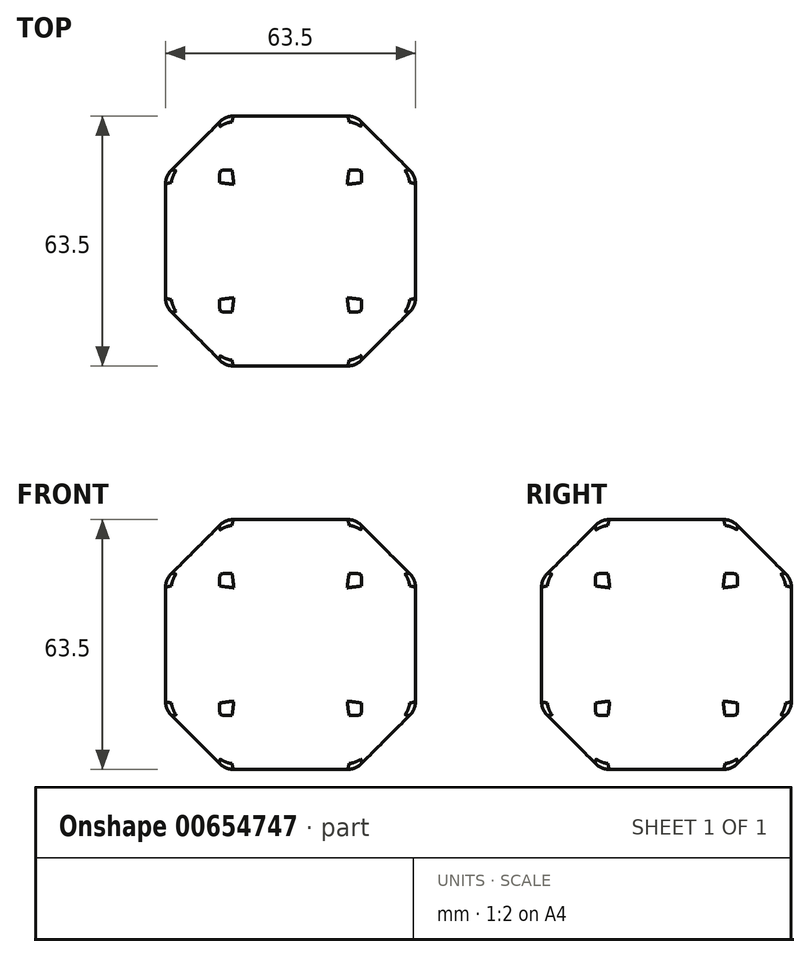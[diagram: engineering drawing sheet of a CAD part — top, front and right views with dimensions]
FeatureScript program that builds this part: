
annotation { "Feature Type Name" : "Feature", "Feature Type Description" : "" }
export const myFeature = defineFeature(function(context is Context, id is Id, definition is map)
    precondition{}
    {
        {
            var Q0;
            Q0=qCreatedBy(makeId("Top.planeOp"),FACE);
            var sketch = newSketch(context, id + "F0", { "sketchPlane" : qUnion([Q0])});
            skLineSegment(sketch, "E0.bottom", {"start": v(-31.75, 31.75) * mm, "end": v(31.75, 31.75) * mm});
            skLineSegment(sketch, "E0.top", {"start": v(-31.75, -31.75) * mm, "end": v(31.75, -31.75) * mm});
            skLineSegment(sketch, "E0.left", {"start": v(-31.75, 31.75) * mm, "end": v(-31.75, -31.75) * mm});
            skLineSegment(sketch, "E0.right", {"start": v(31.75, 31.75) * mm, "end": v(31.75, -31.75) * mm});
            skSolve(sketch);
        }
        {
            var Q0;
            Q0=makeQuery(id+"F0.imprint","IMPRINT",FACE,{"disambiguationData":[TD([[makeQuery(id+"F0.imprint","IMPRINT",EDGE,{"derivedFrom":sQuery(id+"F0.wireOp",EDGE,"E0.bottom")}),-1.0]])]});
            extrude(context, id + "F1", {"entities" : qUnion([Q0]), "depth" : 31.75 * mm, "offsetDistance" : 25.4 * mm, "hasSecondDirection" : true, "secondDirectionOppositeDirection" : true, "secondDirectionDepth" : 31.75 * mm});
        }
        {
            var Q0;
            Q0=makeQuery(id+"F1.opExtrude","CAP_EDGE",EDGE,{"disambiguationData":[OSD([sQuery(id+"F0.wireOp",EDGE,"E0.right")])],"isStart":false});
            var Q1;
            Q1=makeQuery(id+"F1.opExtrude","CAP_EDGE",EDGE,{"disambiguationData":[OSD([sQuery(id+"F0.wireOp",EDGE,"E0.top")])],"isStart":false});
            var Q2;
            Q2=makeQuery(id+"F1.opExtrude","CAP_EDGE",EDGE,{"disambiguationData":[OSD([sQuery(id+"F0.wireOp",EDGE,"E0.left")])],"isStart":false});
            var Q3;
            Q3=makeQuery(id+"F1.opExtrude","CAP_EDGE",EDGE,{"disambiguationData":[OSD([sQuery(id+"F0.wireOp",EDGE,"E0.bottom")])],"isStart":false});
            var Q4;
            Q4=makeQuery(id+"F1.opExtrude","CAP_EDGE",EDGE,{"disambiguationData":[OSD([sQuery(id+"F0.wireOp",EDGE,"E0.top")])],"isStart":true});
            var Q5;
            Q5=makeQuery(id+"F1.opExtrude","CAP_EDGE",EDGE,{"disambiguationData":[OSD([sQuery(id+"F0.wireOp",EDGE,"E0.right")])],"isStart":true});
            var Q6;
            Q6=makeQuery(id+"F1.opExtrude","CAP_EDGE",EDGE,{"disambiguationData":[OSD([sQuery(id+"F0.wireOp",EDGE,"E0.bottom")])],"isStart":true});
            var Q7;
            Q7=makeQuery(id+"F1.opExtrude","CAP_EDGE",EDGE,{"disambiguationData":[OSD([sQuery(id+"F0.wireOp",EDGE,"E0.left")])],"isStart":true});
            var Q8;
            Q8=makeQuery(id+"F1.opExtrude","SWEPT_EDGE",EDGE,{"disambiguationData":[OSD([sQuery(id+"F0.wireOp",EDGE,"E0.bottom"),sQuery(id+"F0.wireOp",EDGE,"E0.left")])]});
            var Q9;
            Q9=makeQuery(id+"F1.opExtrude","SWEPT_EDGE",EDGE,{"disambiguationData":[OSD([sQuery(id+"F0.wireOp",EDGE,"E0.bottom"),sQuery(id+"F0.wireOp",EDGE,"E0.right")])]});
            var Q10;
            Q10=makeQuery(id+"F1.opExtrude","SWEPT_EDGE",EDGE,{"disambiguationData":[OSD([sQuery(id+"F0.wireOp",EDGE,"E0.top"),sQuery(id+"F0.wireOp",EDGE,"E0.right")])]});
            var Q11;
            Q11=makeQuery(id+"F1.opExtrude","SWEPT_EDGE",EDGE,{"disambiguationData":[OSD([sQuery(id+"F0.wireOp",EDGE,"E0.top"),sQuery(id+"F0.wireOp",EDGE,"E0.left")])]});
            chamfer(context, id + "F2", {"entities" : qUnion([Q0, Q1, Q2, Q3, Q4, Q5, Q6, Q7, Q8, Q9, Q10, Q11]), "width" : 15.24 * mm, "tangentPropagation" : true});
        }
        {
            var Q0;
            {var subQ0=sQuery(id+"F0.wireOp",EDGE,"E0.left");Q0=makeQuery(id+"F2.opChamfer","BLEND_EDGE",EDGE,{"blendedFrom":[makeQuery(id+"F1.opExtrude","CAP_VERTEX",VERTEX,{"disambiguationData":[OSD([sQuery(id+"F0.wireOp",EDGE,"E0.bottom"),subQ0])],"isStart":false}),makeQuery(id+"F1.opExtrude","CAP_EDGE",EDGE,{"disambiguationData":[OSD([subQ0])],"isStart":false})],"blendedInto":[]});}
            var Q1;
            {var subQ0=sQuery(id+"F0.wireOp",EDGE,"E0.left");var subQ1=sQuery(id+"F0.wireOp",EDGE,"E0.bottom");Q1=makeQuery(id+"F2.opChamfer","BLEND_FACE",FACE,{"disambiguationData":[OSD([subQ1,subQ0]),TDD([makeQuery(id+"F1.opExtrude","CAP_VERTEX",VERTEX,{"disambiguationData":[OSD([subQ1,subQ0])],"isStart":false})])]});}
            var Q2;
            {var subQ0=sQuery(id+"F0.wireOp",EDGE,"E0.left");var subQ1=sQuery(id+"F0.wireOp",EDGE,"E0.bottom");Q2=makeQuery(id+"F2.opChamfer","BLEND_EDGE",EDGE,{"blendedFrom":[makeQuery(id+"F1.opExtrude","CAP_VERTEX",VERTEX,{"disambiguationData":[OSD([subQ1,subQ0])],"isStart":false}),makeQuery(id+"F1.opExtrude","SWEPT_EDGE",EDGE,{"disambiguationData":[OSD([subQ1,subQ0])]})],"blendedInto":[]});}
            var Q3;
            {var subQ0=sQuery(id+"F0.wireOp",EDGE,"E0.right");var subQ1=sQuery(id+"F0.wireOp",EDGE,"E0.bottom");Q3=makeQuery(id+"F2.opChamfer","BLEND_FACE",FACE,{"disambiguationData":[OSD([subQ1,subQ0]),TDD([makeQuery(id+"F1.opExtrude","CAP_VERTEX",VERTEX,{"disambiguationData":[OSD([subQ1,subQ0])],"isStart":true})])]});}
            var Q4;
            {var subQ0=sQuery(id+"F0.wireOp",EDGE,"E0.right");var subQ1=sQuery(id+"F0.wireOp",EDGE,"E0.bottom");Q4=makeQuery(id+"F2.opChamfer","BLEND_FACE",FACE,{"disambiguationData":[OSD([subQ1,subQ0]),TDD([makeQuery(id+"F1.opExtrude","CAP_VERTEX",VERTEX,{"disambiguationData":[OSD([subQ1,subQ0])],"isStart":false})])]});}
            var Q5;
            {var subQ0=sQuery(id+"F0.wireOp",EDGE,"E0.bottom");Q5=makeQuery(id+"F2.opChamfer","BLEND_EDGE",EDGE,{"blendedFrom":[makeQuery(id+"F1.opExtrude","CAP_VERTEX",VERTEX,{"disambiguationData":[OSD([subQ0,sQuery(id+"F0.wireOp",EDGE,"E0.left")])],"isStart":false}),makeQuery(id+"F1.opExtrude","CAP_EDGE",EDGE,{"disambiguationData":[OSD([subQ0])],"isStart":false})],"blendedInto":[]});}
            var Q6;
            {var subQ0=sQuery(id+"F0.wireOp",EDGE,"E0.bottom");Q6=makeQuery(id+"F2.opChamfer","BLEND_FACE",FACE,{"disambiguationData":[OSD([subQ0]),TDD([makeQuery(id+"F1.opExtrude","CAP_EDGE",EDGE,{"disambiguationData":[OSD([subQ0])],"isStart":false})])]});}
            var Q7;
            {var subQ0=sQuery(id+"F0.wireOp",EDGE,"E0.top");Q7=makeQuery(id+"F2.opChamfer","BLEND_FACE",FACE,{"disambiguationData":[OSD([subQ0]),TDD([makeQuery(id+"F1.opExtrude","CAP_EDGE",EDGE,{"disambiguationData":[OSD([subQ0])],"isStart":false})])]});}
            var Q8;
            {var subQ0=sQuery(id+"F0.wireOp",EDGE,"E0.left");var subQ1=sQuery(id+"F0.wireOp",EDGE,"E0.top");Q8=makeQuery(id+"F2.opChamfer","BLEND_FACE",FACE,{"disambiguationData":[OSD([subQ1,subQ0]),TDD([makeQuery(id+"F1.opExtrude","CAP_VERTEX",VERTEX,{"disambiguationData":[OSD([subQ1,subQ0])],"isStart":false})])]});}
            var Q9;
            {var subQ0=sQuery(id+"F0.wireOp",EDGE,"E0.right");var subQ1=sQuery(id+"F0.wireOp",EDGE,"E0.top");Q9=makeQuery(id+"F2.opChamfer","BLEND_FACE",FACE,{"disambiguationData":[OSD([subQ1,subQ0]),TDD([makeQuery(id+"F1.opExtrude","CAP_VERTEX",VERTEX,{"disambiguationData":[OSD([subQ1,subQ0])],"isStart":true})])]});}
            var Q10;
            {var subQ0=sQuery(id+"F0.wireOp",EDGE,"E0.bottom");Q10=makeQuery(id+"F2.opChamfer","BLEND_EDGE",EDGE,{"blendedFrom":[makeQuery(id+"F1.opExtrude","CAP_VERTEX",VERTEX,{"disambiguationData":[OSD([subQ0,sQuery(id+"F0.wireOp",EDGE,"E0.right")])],"isStart":true}),makeQuery(id+"F1.opExtrude","CAP_EDGE",EDGE,{"disambiguationData":[OSD([subQ0])],"isStart":true})],"blendedInto":[]});}
            var Q11;
            {var subQ0=sQuery(id+"F0.wireOp",EDGE,"E0.right");var subQ1=sQuery(id+"F0.wireOp",EDGE,"E0.top");Q11=makeQuery(id+"F2.opChamfer","BLEND_FACE",FACE,{"disambiguationData":[OSD([subQ1,subQ0]),TDD([makeQuery(id+"F1.opExtrude","CAP_VERTEX",VERTEX,{"disambiguationData":[OSD([subQ1,subQ0])],"isStart":false})])]});}
            var Q12;
            {var subQ0=sQuery(id+"F0.wireOp",EDGE,"E0.right");Q12=makeQuery(id+"F2.opChamfer","BLEND_EDGE",EDGE,{"blendedFrom":[makeQuery(id+"F1.opExtrude","CAP_VERTEX",VERTEX,{"disambiguationData":[OSD([sQuery(id+"F0.wireOp",EDGE,"E0.bottom"),subQ0])],"isStart":true}),makeQuery(id+"F1.opExtrude","CAP_EDGE",EDGE,{"disambiguationData":[OSD([subQ0])],"isStart":true})],"blendedInto":[]});}
            var Q13;
            {var subQ0=sQuery(id+"F0.wireOp",EDGE,"E0.right");var subQ1=sQuery(id+"F0.wireOp",EDGE,"E0.bottom");Q13=makeQuery(id+"F2.opChamfer","BLEND_FACE",FACE,{"disambiguationData":[OSD([subQ1,subQ0]),TDD([makeQuery(id+"F1.opExtrude","SWEPT_EDGE",EDGE,{"disambiguationData":[OSD([subQ1,subQ0])]})])]});}
            var Q14;
            {var subQ0=sQuery(id+"F0.wireOp",EDGE,"E0.bottom");Q14=makeQuery(id+"F2.opChamfer","BLEND_EDGE",EDGE,{"blendedFrom":[makeQuery(id+"F1.opExtrude","CAP_VERTEX",VERTEX,{"disambiguationData":[OSD([subQ0,sQuery(id+"F0.wireOp",EDGE,"E0.right")])],"isStart":false}),makeQuery(id+"F1.opExtrude","CAP_EDGE",EDGE,{"disambiguationData":[OSD([subQ0])],"isStart":false})],"blendedInto":[]});}
            var Q15;
            {var subQ0=sQuery(id+"F0.wireOp",EDGE,"E0.right");Q15=makeQuery(id+"F2.opChamfer","BLEND_EDGE",EDGE,{"blendedFrom":[makeQuery(id+"F1.opExtrude","CAP_VERTEX",VERTEX,{"disambiguationData":[OSD([sQuery(id+"F0.wireOp",EDGE,"E0.bottom"),subQ0])],"isStart":false}),makeQuery(id+"F1.opExtrude","CAP_EDGE",EDGE,{"disambiguationData":[OSD([subQ0])],"isStart":false})],"blendedInto":[]});}
            var Q16;
            {var subQ0=sQuery(id+"F0.wireOp",EDGE,"E0.right");var subQ1=sQuery(id+"F0.wireOp",EDGE,"E0.top");Q16=makeQuery(id+"F2.opChamfer","BLEND_FACE",FACE,{"disambiguationData":[OSD([subQ1,subQ0]),TDD([makeQuery(id+"F1.opExtrude","SWEPT_EDGE",EDGE,{"disambiguationData":[OSD([subQ1,subQ0])]})])]});}
            var Q17;
            {var subQ0=sQuery(id+"F0.wireOp",EDGE,"E0.bottom");Q17=makeQuery(id+"F2.opChamfer","BLEND_FACE",FACE,{"disambiguationData":[OSD([subQ0]),TDD([makeQuery(id+"F1.opExtrude","CAP_EDGE",EDGE,{"disambiguationData":[OSD([subQ0])],"isStart":true})])]});}
            var Q18;
            {var subQ0=sQuery(id+"F0.wireOp",EDGE,"E0.right");Q18=makeQuery(id+"F2.opChamfer","BLEND_EDGE",EDGE,{"blendedFrom":[makeQuery(id+"F1.opExtrude","CAP_EDGE",EDGE,{"disambiguationData":[OSD([subQ0])],"isStart":true}),makeQuery(id+"F1.opExtrude","SWEPT_FACE",FACE,{"disambiguationData":[OSD([subQ0])]})],"blendedInto":[makeQuery(id+"F1.opExtrude","SWEPT_FACE",FACE,{"disambiguationData":[OSD([subQ0])]})]});}
            var Q19;
            {var subQ0=sQuery(id+"F0.wireOp",EDGE,"E0.right");Q19=makeQuery(id+"F2.opChamfer","BLEND_EDGE",EDGE,{"blendedFrom":[makeQuery(id+"F1.opExtrude","CAP_EDGE",EDGE,{"disambiguationData":[OSD([subQ0])],"isStart":false}),makeQuery(id+"F1.opExtrude","CAP_FACE",FACE,{"disambiguationData":[OSD([sQuery(id+"F0.wireOp",EDGE,"E0.bottom"),sQuery(id+"F0.wireOp",EDGE,"E0.top"),sQuery(id+"F0.wireOp",EDGE,"E0.left"),subQ0])],"isStart":false})],"blendedInto":[makeQuery(id+"F1.opExtrude","CAP_FACE",FACE,{"disambiguationData":[OSD([sQuery(id+"F0.wireOp",EDGE,"E0.bottom"),sQuery(id+"F0.wireOp",EDGE,"E0.top"),sQuery(id+"F0.wireOp",EDGE,"E0.left"),subQ0])],"isStart":false})]});}
            var Q20;
            {var subQ0=sQuery(id+"F0.wireOp",EDGE,"E0.right");Q20=makeQuery(id+"F2.opChamfer","BLEND_EDGE",EDGE,{"blendedFrom":[makeQuery(id+"F1.opExtrude","CAP_EDGE",EDGE,{"disambiguationData":[OSD([subQ0])],"isStart":false}),makeQuery(id+"F1.opExtrude","SWEPT_FACE",FACE,{"disambiguationData":[OSD([subQ0])]})],"blendedInto":[makeQuery(id+"F1.opExtrude","SWEPT_FACE",FACE,{"disambiguationData":[OSD([subQ0])]})]});}
            var Q21;
            {var subQ0=sQuery(id+"F0.wireOp",EDGE,"E0.top");Q21=makeQuery(id+"F2.opChamfer","BLEND_EDGE",EDGE,{"blendedFrom":[makeQuery(id+"F1.opExtrude","CAP_VERTEX",VERTEX,{"disambiguationData":[OSD([subQ0,sQuery(id+"F0.wireOp",EDGE,"E0.left")])],"isStart":false}),makeQuery(id+"F1.opExtrude","CAP_EDGE",EDGE,{"disambiguationData":[OSD([subQ0])],"isStart":false})],"blendedInto":[]});}
            var Q22;
            {var subQ0=sQuery(id+"F0.wireOp",EDGE,"E0.bottom");Q22=makeQuery(id+"F2.opChamfer","BLEND_EDGE",EDGE,{"blendedFrom":[makeQuery(id+"F1.opExtrude","CAP_EDGE",EDGE,{"disambiguationData":[OSD([subQ0])],"isStart":true}),makeQuery(id+"F1.opExtrude","SWEPT_FACE",FACE,{"disambiguationData":[OSD([subQ0])]})],"blendedInto":[makeQuery(id+"F1.opExtrude","SWEPT_FACE",FACE,{"disambiguationData":[OSD([subQ0])]})]});}
            var Q23;
            {var subQ0=sQuery(id+"F0.wireOp",EDGE,"E0.right");var subQ1=sQuery(id+"F0.wireOp",EDGE,"E0.top");Q23=makeQuery(id+"F2.opChamfer","BLEND_EDGE",EDGE,{"blendedFrom":[makeQuery(id+"F1.opExtrude","CAP_VERTEX",VERTEX,{"disambiguationData":[OSD([subQ1,subQ0])],"isStart":true}),makeQuery(id+"F1.opExtrude","SWEPT_EDGE",EDGE,{"disambiguationData":[OSD([subQ1,subQ0])]})],"blendedInto":[]});}
            var Q24;
            {var subQ0=sQuery(id+"F0.wireOp",EDGE,"E0.bottom");Q24=makeQuery(id+"F2.opChamfer","BLEND_EDGE",EDGE,{"blendedFrom":[makeQuery(id+"F1.opExtrude","CAP_EDGE",EDGE,{"disambiguationData":[OSD([subQ0])],"isStart":false}),makeQuery(id+"F1.opExtrude","SWEPT_FACE",FACE,{"disambiguationData":[OSD([subQ0])]})],"blendedInto":[makeQuery(id+"F1.opExtrude","SWEPT_FACE",FACE,{"disambiguationData":[OSD([subQ0])]})]});}
            var Q25;
            {var subQ0=sQuery(id+"F0.wireOp",EDGE,"E0.right");Q25=makeQuery(id+"F2.opChamfer","BLEND_FACE",FACE,{"disambiguationData":[OSD([subQ0]),TDD([makeQuery(id+"F1.opExtrude","CAP_EDGE",EDGE,{"disambiguationData":[OSD([subQ0])],"isStart":true})])]});}
            var Q26;
            {var subQ0=sQuery(id+"F0.wireOp",EDGE,"E0.bottom");Q26=makeQuery(id+"F2.opChamfer","BLEND_EDGE",EDGE,{"blendedFrom":[makeQuery(id+"F1.opExtrude","CAP_EDGE",EDGE,{"disambiguationData":[OSD([subQ0])],"isStart":false}),makeQuery(id+"F1.opExtrude","CAP_FACE",FACE,{"disambiguationData":[OSD([subQ0,sQuery(id+"F0.wireOp",EDGE,"E0.top"),sQuery(id+"F0.wireOp",EDGE,"E0.left"),sQuery(id+"F0.wireOp",EDGE,"E0.right")])],"isStart":false})],"blendedInto":[makeQuery(id+"F1.opExtrude","CAP_FACE",FACE,{"disambiguationData":[OSD([subQ0,sQuery(id+"F0.wireOp",EDGE,"E0.top"),sQuery(id+"F0.wireOp",EDGE,"E0.left"),sQuery(id+"F0.wireOp",EDGE,"E0.right")])],"isStart":false})]});}
            var Q27;
            {var subQ0=sQuery(id+"F0.wireOp",EDGE,"E0.right");Q27=makeQuery(id+"F2.opChamfer","BLEND_FACE",FACE,{"disambiguationData":[OSD([subQ0]),TDD([makeQuery(id+"F1.opExtrude","CAP_EDGE",EDGE,{"disambiguationData":[OSD([subQ0])],"isStart":false})])]});}
            var Q28;
            {var subQ0=sQuery(id+"F0.wireOp",EDGE,"E0.right");Q28=makeQuery(id+"F2.opChamfer","BLEND_EDGE",EDGE,{"blendedFrom":[makeQuery(id+"F1.opExtrude","CAP_VERTEX",VERTEX,{"disambiguationData":[OSD([sQuery(id+"F0.wireOp",EDGE,"E0.top"),subQ0])],"isStart":true}),makeQuery(id+"F1.opExtrude","CAP_EDGE",EDGE,{"disambiguationData":[OSD([subQ0])],"isStart":true})],"blendedInto":[]});}
            var Q29;
            Q29=makeQuery(id+"F1.opExtrude","SWEPT_FACE",FACE,{"disambiguationData":[OSD([sQuery(id+"F0.wireOp",EDGE,"E0.bottom")])]});
            var Q30;
            {var subQ0=sQuery(id+"F0.wireOp",EDGE,"E0.right");var subQ1=sQuery(id+"F0.wireOp",EDGE,"E0.top");Q30=makeQuery(id+"F2.opChamfer","BLEND_EDGE",EDGE,{"blendedFrom":[makeQuery(id+"F1.opExtrude","CAP_VERTEX",VERTEX,{"disambiguationData":[OSD([subQ1,subQ0])],"isStart":false}),makeQuery(id+"F1.opExtrude","SWEPT_EDGE",EDGE,{"disambiguationData":[OSD([subQ1,subQ0])]})],"blendedInto":[]});}
            var Q31;
            {var subQ0=sQuery(id+"F0.wireOp",EDGE,"E0.top");Q31=makeQuery(id+"F2.opChamfer","BLEND_EDGE",EDGE,{"blendedFrom":[makeQuery(id+"F1.opExtrude","CAP_VERTEX",VERTEX,{"disambiguationData":[OSD([subQ0,sQuery(id+"F0.wireOp",EDGE,"E0.right")])],"isStart":false}),makeQuery(id+"F1.opExtrude","CAP_EDGE",EDGE,{"disambiguationData":[OSD([subQ0])],"isStart":false})],"blendedInto":[]});}
            var Q32;
            {var subQ0=sQuery(id+"F0.wireOp",EDGE,"E0.top");Q32=makeQuery(id+"F2.opChamfer","BLEND_EDGE",EDGE,{"blendedFrom":[makeQuery(id+"F1.opExtrude","CAP_EDGE",EDGE,{"disambiguationData":[OSD([subQ0])],"isStart":false}),makeQuery(id+"F1.opExtrude","CAP_FACE",FACE,{"disambiguationData":[OSD([sQuery(id+"F0.wireOp",EDGE,"E0.bottom"),subQ0,sQuery(id+"F0.wireOp",EDGE,"E0.left"),sQuery(id+"F0.wireOp",EDGE,"E0.right")])],"isStart":false})],"blendedInto":[makeQuery(id+"F1.opExtrude","CAP_FACE",FACE,{"disambiguationData":[OSD([sQuery(id+"F0.wireOp",EDGE,"E0.bottom"),subQ0,sQuery(id+"F0.wireOp",EDGE,"E0.left"),sQuery(id+"F0.wireOp",EDGE,"E0.right")])],"isStart":false})]});}
            var Q33;
            Q33=makeQuery(id+"F1.opExtrude","CAP_FACE",FACE,{"disambiguationData":[OSD([sQuery(id+"F0.wireOp",EDGE,"E0.bottom"),sQuery(id+"F0.wireOp",EDGE,"E0.top"),sQuery(id+"F0.wireOp",EDGE,"E0.left"),sQuery(id+"F0.wireOp",EDGE,"E0.right")])],"isStart":false});
            var Q34;
            {var subQ0=sQuery(id+"F0.wireOp",EDGE,"E0.right");Q34=makeQuery(id+"F2.opChamfer","BLEND_EDGE",EDGE,{"blendedFrom":[makeQuery(id+"F1.opExtrude","CAP_VERTEX",VERTEX,{"disambiguationData":[OSD([sQuery(id+"F0.wireOp",EDGE,"E0.top"),subQ0])],"isStart":false}),makeQuery(id+"F1.opExtrude","CAP_EDGE",EDGE,{"disambiguationData":[OSD([subQ0])],"isStart":false})],"blendedInto":[]});}
            var Q35;
            {var subQ0=sQuery(id+"F0.wireOp",EDGE,"E0.top");Q35=makeQuery(id+"F2.opChamfer","BLEND_EDGE",EDGE,{"blendedFrom":[makeQuery(id+"F1.opExtrude","CAP_EDGE",EDGE,{"disambiguationData":[OSD([subQ0])],"isStart":false}),makeQuery(id+"F1.opExtrude","SWEPT_FACE",FACE,{"disambiguationData":[OSD([subQ0])]})],"blendedInto":[makeQuery(id+"F1.opExtrude","SWEPT_FACE",FACE,{"disambiguationData":[OSD([subQ0])]})]});}
            var Q36;
            Q36=makeQuery(id+"F1.opExtrude","SWEPT_FACE",FACE,{"disambiguationData":[OSD([sQuery(id+"F0.wireOp",EDGE,"E0.top")])]});
            var Q37;
            Q37=makeQuery(id+"F1.opExtrude","SWEPT_FACE",FACE,{"disambiguationData":[OSD([sQuery(id+"F0.wireOp",EDGE,"E0.right")])]});
            var Q38;
            {var subQ0=sQuery(id+"F0.wireOp",EDGE,"E0.left");Q38=makeQuery(id+"F2.opChamfer","BLEND_EDGE",EDGE,{"blendedFrom":[makeQuery(id+"F1.opExtrude","CAP_EDGE",EDGE,{"disambiguationData":[OSD([subQ0])],"isStart":false}),makeQuery(id+"F1.opExtrude","CAP_FACE",FACE,{"disambiguationData":[OSD([sQuery(id+"F0.wireOp",EDGE,"E0.bottom"),sQuery(id+"F0.wireOp",EDGE,"E0.top"),subQ0,sQuery(id+"F0.wireOp",EDGE,"E0.right")])],"isStart":false})],"blendedInto":[makeQuery(id+"F1.opExtrude","CAP_FACE",FACE,{"disambiguationData":[OSD([sQuery(id+"F0.wireOp",EDGE,"E0.bottom"),sQuery(id+"F0.wireOp",EDGE,"E0.top"),subQ0,sQuery(id+"F0.wireOp",EDGE,"E0.right")])],"isStart":false})]});}
            var Q39;
            {var subQ0=sQuery(id+"F0.wireOp",EDGE,"E0.right");Q39=makeQuery(id+"F2.opChamfer","BLEND_EDGE",EDGE,{"blendedFrom":[makeQuery(id+"F1.opExtrude","CAP_EDGE",EDGE,{"disambiguationData":[OSD([subQ0])],"isStart":true}),makeQuery(id+"F1.opExtrude","CAP_FACE",FACE,{"disambiguationData":[OSD([sQuery(id+"F0.wireOp",EDGE,"E0.bottom"),sQuery(id+"F0.wireOp",EDGE,"E0.top"),sQuery(id+"F0.wireOp",EDGE,"E0.left"),subQ0])],"isStart":true})],"blendedInto":[makeQuery(id+"F1.opExtrude","CAP_FACE",FACE,{"disambiguationData":[OSD([sQuery(id+"F0.wireOp",EDGE,"E0.bottom"),sQuery(id+"F0.wireOp",EDGE,"E0.top"),sQuery(id+"F0.wireOp",EDGE,"E0.left"),subQ0])],"isStart":true})]});}
            var Q40;
            {var subQ0=sQuery(id+"F0.wireOp",EDGE,"E0.left");var subQ1=sQuery(id+"F0.wireOp",EDGE,"E0.top");Q40=makeQuery(id+"F2.opChamfer","BLEND_FACE",FACE,{"disambiguationData":[OSD([subQ1,subQ0]),TDD([makeQuery(id+"F1.opExtrude","CAP_VERTEX",VERTEX,{"disambiguationData":[OSD([subQ1,subQ0])],"isStart":true})])]});}
            var Q41;
            {var subQ0=sQuery(id+"F0.wireOp",EDGE,"E0.left");Q41=makeQuery(id+"F2.opChamfer","BLEND_EDGE",EDGE,{"blendedFrom":[makeQuery(id+"F1.opExtrude","CAP_VERTEX",VERTEX,{"disambiguationData":[OSD([sQuery(id+"F0.wireOp",EDGE,"E0.bottom"),subQ0])],"isStart":true}),makeQuery(id+"F1.opExtrude","CAP_EDGE",EDGE,{"disambiguationData":[OSD([subQ0])],"isStart":true})],"blendedInto":[]});}
            var Q42;
            {var subQ0=sQuery(id+"F0.wireOp",EDGE,"E0.bottom");Q42=makeQuery(id+"F2.opChamfer","BLEND_EDGE",EDGE,{"blendedFrom":[makeQuery(id+"F1.opExtrude","CAP_VERTEX",VERTEX,{"disambiguationData":[OSD([subQ0,sQuery(id+"F0.wireOp",EDGE,"E0.left")])],"isStart":true}),makeQuery(id+"F1.opExtrude","CAP_EDGE",EDGE,{"disambiguationData":[OSD([subQ0])],"isStart":true})],"blendedInto":[]});}
            var Q43;
            {var subQ0=sQuery(id+"F0.wireOp",EDGE,"E0.left");var subQ1=sQuery(id+"F0.wireOp",EDGE,"E0.bottom");Q43=makeQuery(id+"F2.opChamfer","BLEND_FACE",FACE,{"disambiguationData":[OSD([subQ1,subQ0]),TDD([makeQuery(id+"F1.opExtrude","CAP_VERTEX",VERTEX,{"disambiguationData":[OSD([subQ1,subQ0])],"isStart":true})])]});}
            var Q44;
            {var subQ0=sQuery(id+"F0.wireOp",EDGE,"E0.left");var subQ1=sQuery(id+"F0.wireOp",EDGE,"E0.bottom");Q44=makeQuery(id+"F2.opChamfer","BLEND_EDGE",EDGE,{"blendedFrom":[makeQuery(id+"F1.opExtrude","CAP_VERTEX",VERTEX,{"disambiguationData":[OSD([subQ1,subQ0])],"isStart":true}),makeQuery(id+"F1.opExtrude","SWEPT_EDGE",EDGE,{"disambiguationData":[OSD([subQ1,subQ0])]})],"blendedInto":[]});}
            var Q45;
            {var subQ0=sQuery(id+"F0.wireOp",EDGE,"E0.top");Q45=makeQuery(id+"F2.opChamfer","BLEND_FACE",FACE,{"disambiguationData":[OSD([subQ0]),TDD([makeQuery(id+"F1.opExtrude","CAP_EDGE",EDGE,{"disambiguationData":[OSD([subQ0])],"isStart":true})])]});}
            var Q46;
            {var subQ0=sQuery(id+"F0.wireOp",EDGE,"E0.left");Q46=makeQuery(id+"F2.opChamfer","BLEND_EDGE",EDGE,{"blendedFrom":[makeQuery(id+"F1.opExtrude","CAP_VERTEX",VERTEX,{"disambiguationData":[OSD([sQuery(id+"F0.wireOp",EDGE,"E0.top"),subQ0])],"isStart":true}),makeQuery(id+"F1.opExtrude","CAP_EDGE",EDGE,{"disambiguationData":[OSD([subQ0])],"isStart":true})],"blendedInto":[]});}
            var Q47;
            {var subQ0=sQuery(id+"F0.wireOp",EDGE,"E0.top");Q47=makeQuery(id+"F2.opChamfer","BLEND_EDGE",EDGE,{"blendedFrom":[makeQuery(id+"F1.opExtrude","CAP_VERTEX",VERTEX,{"disambiguationData":[OSD([subQ0,sQuery(id+"F0.wireOp",EDGE,"E0.left")])],"isStart":true}),makeQuery(id+"F1.opExtrude","CAP_EDGE",EDGE,{"disambiguationData":[OSD([subQ0])],"isStart":true})],"blendedInto":[]});}
            var Q48;
            {var subQ0=sQuery(id+"F0.wireOp",EDGE,"E0.right");var subQ1=sQuery(id+"F0.wireOp",EDGE,"E0.bottom");Q48=makeQuery(id+"F2.opChamfer","BLEND_EDGE",EDGE,{"blendedFrom":[makeQuery(id+"F1.opExtrude","CAP_VERTEX",VERTEX,{"disambiguationData":[OSD([subQ1,subQ0])],"isStart":true}),makeQuery(id+"F1.opExtrude","SWEPT_EDGE",EDGE,{"disambiguationData":[OSD([subQ1,subQ0])]})],"blendedInto":[]});}
            var Q49;
            {var subQ0=sQuery(id+"F0.wireOp",EDGE,"E0.left");var subQ1=sQuery(id+"F0.wireOp",EDGE,"E0.bottom");Q49=makeQuery(id+"F2.opChamfer","BLEND_FACE",FACE,{"disambiguationData":[OSD([subQ1,subQ0]),TDD([makeQuery(id+"F1.opExtrude","SWEPT_EDGE",EDGE,{"disambiguationData":[OSD([subQ1,subQ0])]})])]});}
            var Q50;
            {var subQ0=sQuery(id+"F0.wireOp",EDGE,"E0.right");var subQ1=sQuery(id+"F0.wireOp",EDGE,"E0.bottom");Q50=makeQuery(id+"F2.opChamfer","BLEND_EDGE",EDGE,{"blendedFrom":[makeQuery(id+"F1.opExtrude","CAP_VERTEX",VERTEX,{"disambiguationData":[OSD([subQ1,subQ0])],"isStart":false}),makeQuery(id+"F1.opExtrude","SWEPT_EDGE",EDGE,{"disambiguationData":[OSD([subQ1,subQ0])]})],"blendedInto":[]});}
            var Q51;
            {var subQ0=sQuery(id+"F0.wireOp",EDGE,"E0.left");var subQ1=sQuery(id+"F0.wireOp",EDGE,"E0.top");Q51=makeQuery(id+"F2.opChamfer","BLEND_FACE",FACE,{"disambiguationData":[OSD([subQ1,subQ0]),TDD([makeQuery(id+"F1.opExtrude","SWEPT_EDGE",EDGE,{"disambiguationData":[OSD([subQ1,subQ0])]})])]});}
            var Q52;
            {var subQ0=sQuery(id+"F0.wireOp",EDGE,"E0.top");Q52=makeQuery(id+"F2.opChamfer","BLEND_EDGE",EDGE,{"blendedFrom":[makeQuery(id+"F1.opExtrude","SWEPT_EDGE",EDGE,{"disambiguationData":[OSD([subQ0,sQuery(id+"F0.wireOp",EDGE,"E0.right")])]}),makeQuery(id+"F1.opExtrude","SWEPT_FACE",FACE,{"disambiguationData":[OSD([subQ0])]})],"blendedInto":[makeQuery(id+"F1.opExtrude","SWEPT_FACE",FACE,{"disambiguationData":[OSD([subQ0])]})]});}
            var Q53;
            {var subQ0=sQuery(id+"F0.wireOp",EDGE,"E0.right");Q53=makeQuery(id+"F2.opChamfer","BLEND_EDGE",EDGE,{"blendedFrom":[makeQuery(id+"F1.opExtrude","SWEPT_EDGE",EDGE,{"disambiguationData":[OSD([sQuery(id+"F0.wireOp",EDGE,"E0.top"),subQ0])]}),makeQuery(id+"F1.opExtrude","SWEPT_FACE",FACE,{"disambiguationData":[OSD([subQ0])]})],"blendedInto":[makeQuery(id+"F1.opExtrude","SWEPT_FACE",FACE,{"disambiguationData":[OSD([subQ0])]})]});}
            var Q54;
            {var subQ0=sQuery(id+"F0.wireOp",EDGE,"E0.left");Q54=makeQuery(id+"F2.opChamfer","BLEND_FACE",FACE,{"disambiguationData":[OSD([subQ0]),TDD([makeQuery(id+"F1.opExtrude","CAP_EDGE",EDGE,{"disambiguationData":[OSD([subQ0])],"isStart":true})])]});}
            var Q55;
            {var subQ0=sQuery(id+"F0.wireOp",EDGE,"E0.left");Q55=makeQuery(id+"F2.opChamfer","BLEND_EDGE",EDGE,{"blendedFrom":[makeQuery(id+"F1.opExtrude","CAP_VERTEX",VERTEX,{"disambiguationData":[OSD([sQuery(id+"F0.wireOp",EDGE,"E0.top"),subQ0])],"isStart":false}),makeQuery(id+"F1.opExtrude","CAP_EDGE",EDGE,{"disambiguationData":[OSD([subQ0])],"isStart":false})],"blendedInto":[]});}
            var Q56;
            {var subQ0=sQuery(id+"F0.wireOp",EDGE,"E0.bottom");Q56=makeQuery(id+"F2.opChamfer","BLEND_EDGE",EDGE,{"blendedFrom":[makeQuery(id+"F1.opExtrude","CAP_EDGE",EDGE,{"disambiguationData":[OSD([subQ0])],"isStart":true}),makeQuery(id+"F1.opExtrude","CAP_FACE",FACE,{"disambiguationData":[OSD([subQ0,sQuery(id+"F0.wireOp",EDGE,"E0.top"),sQuery(id+"F0.wireOp",EDGE,"E0.left"),sQuery(id+"F0.wireOp",EDGE,"E0.right")])],"isStart":true})],"blendedInto":[makeQuery(id+"F1.opExtrude","CAP_FACE",FACE,{"disambiguationData":[OSD([subQ0,sQuery(id+"F0.wireOp",EDGE,"E0.top"),sQuery(id+"F0.wireOp",EDGE,"E0.left"),sQuery(id+"F0.wireOp",EDGE,"E0.right")])],"isStart":true})]});}
            var Q57;
            {var subQ0=sQuery(id+"F0.wireOp",EDGE,"E0.left");Q57=makeQuery(id+"F2.opChamfer","BLEND_FACE",FACE,{"disambiguationData":[OSD([subQ0]),TDD([makeQuery(id+"F1.opExtrude","CAP_EDGE",EDGE,{"disambiguationData":[OSD([subQ0])],"isStart":false})])]});}
            var Q58;
            {var subQ0=sQuery(id+"F0.wireOp",EDGE,"E0.top");Q58=makeQuery(id+"F2.opChamfer","BLEND_EDGE",EDGE,{"blendedFrom":[makeQuery(id+"F1.opExtrude","CAP_VERTEX",VERTEX,{"disambiguationData":[OSD([subQ0,sQuery(id+"F0.wireOp",EDGE,"E0.right")])],"isStart":true}),makeQuery(id+"F1.opExtrude","CAP_EDGE",EDGE,{"disambiguationData":[OSD([subQ0])],"isStart":true})],"blendedInto":[]});}
            var Q59;
            {var subQ0=sQuery(id+"F0.wireOp",EDGE,"E0.top");Q59=makeQuery(id+"F2.opChamfer","BLEND_EDGE",EDGE,{"blendedFrom":[makeQuery(id+"F1.opExtrude","CAP_EDGE",EDGE,{"disambiguationData":[OSD([subQ0])],"isStart":true}),makeQuery(id+"F1.opExtrude","CAP_FACE",FACE,{"disambiguationData":[OSD([sQuery(id+"F0.wireOp",EDGE,"E0.bottom"),subQ0,sQuery(id+"F0.wireOp",EDGE,"E0.left"),sQuery(id+"F0.wireOp",EDGE,"E0.right")])],"isStart":true})],"blendedInto":[makeQuery(id+"F1.opExtrude","CAP_FACE",FACE,{"disambiguationData":[OSD([sQuery(id+"F0.wireOp",EDGE,"E0.bottom"),subQ0,sQuery(id+"F0.wireOp",EDGE,"E0.left"),sQuery(id+"F0.wireOp",EDGE,"E0.right")])],"isStart":true})]});}
            var Q60;
            {var subQ0=sQuery(id+"F0.wireOp",EDGE,"E0.top");Q60=makeQuery(id+"F2.opChamfer","BLEND_EDGE",EDGE,{"blendedFrom":[makeQuery(id+"F1.opExtrude","CAP_EDGE",EDGE,{"disambiguationData":[OSD([subQ0])],"isStart":true}),makeQuery(id+"F1.opExtrude","SWEPT_FACE",FACE,{"disambiguationData":[OSD([subQ0])]})],"blendedInto":[makeQuery(id+"F1.opExtrude","SWEPT_FACE",FACE,{"disambiguationData":[OSD([subQ0])]})]});}
            var Q61;
            Q61=makeQuery(id+"F1.opExtrude","CAP_FACE",FACE,{"disambiguationData":[OSD([sQuery(id+"F0.wireOp",EDGE,"E0.bottom"),sQuery(id+"F0.wireOp",EDGE,"E0.top"),sQuery(id+"F0.wireOp",EDGE,"E0.left"),sQuery(id+"F0.wireOp",EDGE,"E0.right")])],"isStart":true});
            var Q62;
            {var subQ0=sQuery(id+"F0.wireOp",EDGE,"E0.bottom");Q62=makeQuery(id+"F2.opChamfer","BLEND_EDGE",EDGE,{"blendedFrom":[makeQuery(id+"F1.opExtrude","SWEPT_EDGE",EDGE,{"disambiguationData":[OSD([subQ0,sQuery(id+"F0.wireOp",EDGE,"E0.left")])]}),makeQuery(id+"F1.opExtrude","SWEPT_FACE",FACE,{"disambiguationData":[OSD([subQ0])]})],"blendedInto":[makeQuery(id+"F1.opExtrude","SWEPT_FACE",FACE,{"disambiguationData":[OSD([subQ0])]})]});}
            var Q63;
            {var subQ0=sQuery(id+"F0.wireOp",EDGE,"E0.left");Q63=makeQuery(id+"F2.opChamfer","BLEND_EDGE",EDGE,{"blendedFrom":[makeQuery(id+"F1.opExtrude","CAP_EDGE",EDGE,{"disambiguationData":[OSD([subQ0])],"isStart":true}),makeQuery(id+"F1.opExtrude","CAP_FACE",FACE,{"disambiguationData":[OSD([sQuery(id+"F0.wireOp",EDGE,"E0.bottom"),sQuery(id+"F0.wireOp",EDGE,"E0.top"),subQ0,sQuery(id+"F0.wireOp",EDGE,"E0.right")])],"isStart":true})],"blendedInto":[makeQuery(id+"F1.opExtrude","CAP_FACE",FACE,{"disambiguationData":[OSD([sQuery(id+"F0.wireOp",EDGE,"E0.bottom"),sQuery(id+"F0.wireOp",EDGE,"E0.top"),subQ0,sQuery(id+"F0.wireOp",EDGE,"E0.right")])],"isStart":true})]});}
            var Q64;
            Q64=makeQuery(id+"F1.opExtrude","SWEPT_FACE",FACE,{"disambiguationData":[OSD([sQuery(id+"F0.wireOp",EDGE,"E0.left")])]});
            var Q65;
            {var subQ0=sQuery(id+"F0.wireOp",EDGE,"E0.left");Q65=makeQuery(id+"F2.opChamfer","BLEND_EDGE",EDGE,{"blendedFrom":[makeQuery(id+"F1.opExtrude","CAP_EDGE",EDGE,{"disambiguationData":[OSD([subQ0])],"isStart":true}),makeQuery(id+"F1.opExtrude","SWEPT_FACE",FACE,{"disambiguationData":[OSD([subQ0])]})],"blendedInto":[makeQuery(id+"F1.opExtrude","SWEPT_FACE",FACE,{"disambiguationData":[OSD([subQ0])]})]});}
            var Q66;
            {var subQ0=sQuery(id+"F0.wireOp",EDGE,"E0.bottom");Q66=makeQuery(id+"F2.opChamfer","BLEND_EDGE",EDGE,{"blendedFrom":[makeQuery(id+"F1.opExtrude","SWEPT_EDGE",EDGE,{"disambiguationData":[OSD([subQ0,sQuery(id+"F0.wireOp",EDGE,"E0.right")])]}),makeQuery(id+"F1.opExtrude","SWEPT_FACE",FACE,{"disambiguationData":[OSD([subQ0])]})],"blendedInto":[makeQuery(id+"F1.opExtrude","SWEPT_FACE",FACE,{"disambiguationData":[OSD([subQ0])]})]});}
            var Q67;
            {var subQ0=sQuery(id+"F0.wireOp",EDGE,"E0.right");Q67=makeQuery(id+"F2.opChamfer","BLEND_EDGE",EDGE,{"blendedFrom":[makeQuery(id+"F1.opExtrude","SWEPT_EDGE",EDGE,{"disambiguationData":[OSD([sQuery(id+"F0.wireOp",EDGE,"E0.bottom"),subQ0])]}),makeQuery(id+"F1.opExtrude","SWEPT_FACE",FACE,{"disambiguationData":[OSD([subQ0])]})],"blendedInto":[makeQuery(id+"F1.opExtrude","SWEPT_FACE",FACE,{"disambiguationData":[OSD([subQ0])]})]});}
            var Q68;
            {var subQ0=sQuery(id+"F0.wireOp",EDGE,"E0.left");Q68=makeQuery(id+"F2.opChamfer","BLEND_EDGE",EDGE,{"blendedFrom":[makeQuery(id+"F1.opExtrude","CAP_EDGE",EDGE,{"disambiguationData":[OSD([subQ0])],"isStart":false}),makeQuery(id+"F1.opExtrude","SWEPT_FACE",FACE,{"disambiguationData":[OSD([subQ0])]})],"blendedInto":[makeQuery(id+"F1.opExtrude","SWEPT_FACE",FACE,{"disambiguationData":[OSD([subQ0])]})]});}
            var Q69;
            {var subQ0=sQuery(id+"F0.wireOp",EDGE,"E0.top");Q69=makeQuery(id+"F2.opChamfer","BLEND_EDGE",EDGE,{"blendedFrom":[makeQuery(id+"F1.opExtrude","SWEPT_EDGE",EDGE,{"disambiguationData":[OSD([subQ0,sQuery(id+"F0.wireOp",EDGE,"E0.left")])]}),makeQuery(id+"F1.opExtrude","SWEPT_FACE",FACE,{"disambiguationData":[OSD([subQ0])]})],"blendedInto":[makeQuery(id+"F1.opExtrude","SWEPT_FACE",FACE,{"disambiguationData":[OSD([subQ0])]})]});}
            var Q70;
            {var subQ0=sQuery(id+"F0.wireOp",EDGE,"E0.left");var subQ1=sQuery(id+"F0.wireOp",EDGE,"E0.top");Q70=makeQuery(id+"F2.opChamfer","BLEND_EDGE",EDGE,{"blendedFrom":[makeQuery(id+"F1.opExtrude","CAP_VERTEX",VERTEX,{"disambiguationData":[OSD([subQ1,subQ0])],"isStart":false}),makeQuery(id+"F1.opExtrude","SWEPT_EDGE",EDGE,{"disambiguationData":[OSD([subQ1,subQ0])]})],"blendedInto":[]});}
            var Q71;
            {var subQ0=sQuery(id+"F0.wireOp",EDGE,"E0.left");var subQ1=sQuery(id+"F0.wireOp",EDGE,"E0.top");Q71=makeQuery(id+"F2.opChamfer","BLEND_EDGE",EDGE,{"blendedFrom":[makeQuery(id+"F1.opExtrude","CAP_VERTEX",VERTEX,{"disambiguationData":[OSD([subQ1,subQ0])],"isStart":true}),makeQuery(id+"F1.opExtrude","SWEPT_EDGE",EDGE,{"disambiguationData":[OSD([subQ1,subQ0])]})],"blendedInto":[]});}
            var Q72;
            {var subQ0=sQuery(id+"F0.wireOp",EDGE,"E0.left");Q72=makeQuery(id+"F2.opChamfer","BLEND_EDGE",EDGE,{"blendedFrom":[makeQuery(id+"F1.opExtrude","SWEPT_EDGE",EDGE,{"disambiguationData":[OSD([sQuery(id+"F0.wireOp",EDGE,"E0.top"),subQ0])]}),makeQuery(id+"F1.opExtrude","SWEPT_FACE",FACE,{"disambiguationData":[OSD([subQ0])]})],"blendedInto":[makeQuery(id+"F1.opExtrude","SWEPT_FACE",FACE,{"disambiguationData":[OSD([subQ0])]})]});}
            var Q73;
            {var subQ0=sQuery(id+"F0.wireOp",EDGE,"E0.left");Q73=makeQuery(id+"F2.opChamfer","BLEND_EDGE",EDGE,{"blendedFrom":[makeQuery(id+"F1.opExtrude","SWEPT_EDGE",EDGE,{"disambiguationData":[OSD([sQuery(id+"F0.wireOp",EDGE,"E0.bottom"),subQ0])]}),makeQuery(id+"F1.opExtrude","SWEPT_FACE",FACE,{"disambiguationData":[OSD([subQ0])]})],"blendedInto":[makeQuery(id+"F1.opExtrude","SWEPT_FACE",FACE,{"disambiguationData":[OSD([subQ0])]})]});}
            fillet(context, id + "F3", {"entities" : qUnion([Q0, Q1, Q2, Q3, Q4, Q5, Q6, Q7, Q8, Q9, Q10, Q11, Q12, Q13, Q14, Q15, Q16, Q17, Q18, Q19, Q20, Q21, Q22, Q23, Q24, Q25, Q26, Q27, Q28, Q29, Q30, Q31, Q32, Q33, Q34, Q35, Q36, Q37, Q38, Q39, Q40, Q41, Q42, Q43, Q44, Q45, Q46, Q47, Q48, Q49, Q50, Q51, Q52, Q53, Q54, Q55, Q56, Q57, Q58, Q59, Q60, Q61, Q62, Q63, Q64, Q65, Q66, Q67, Q68, Q69, Q70, Q71, Q72, Q73]), "radius" : 5.08 * mm, "tangentPropagation" : true, "rho" : 0.5, "crossSection" : FilletCrossSection.CONIC, "allowEdgeOverflow" : false});
        }
    });
